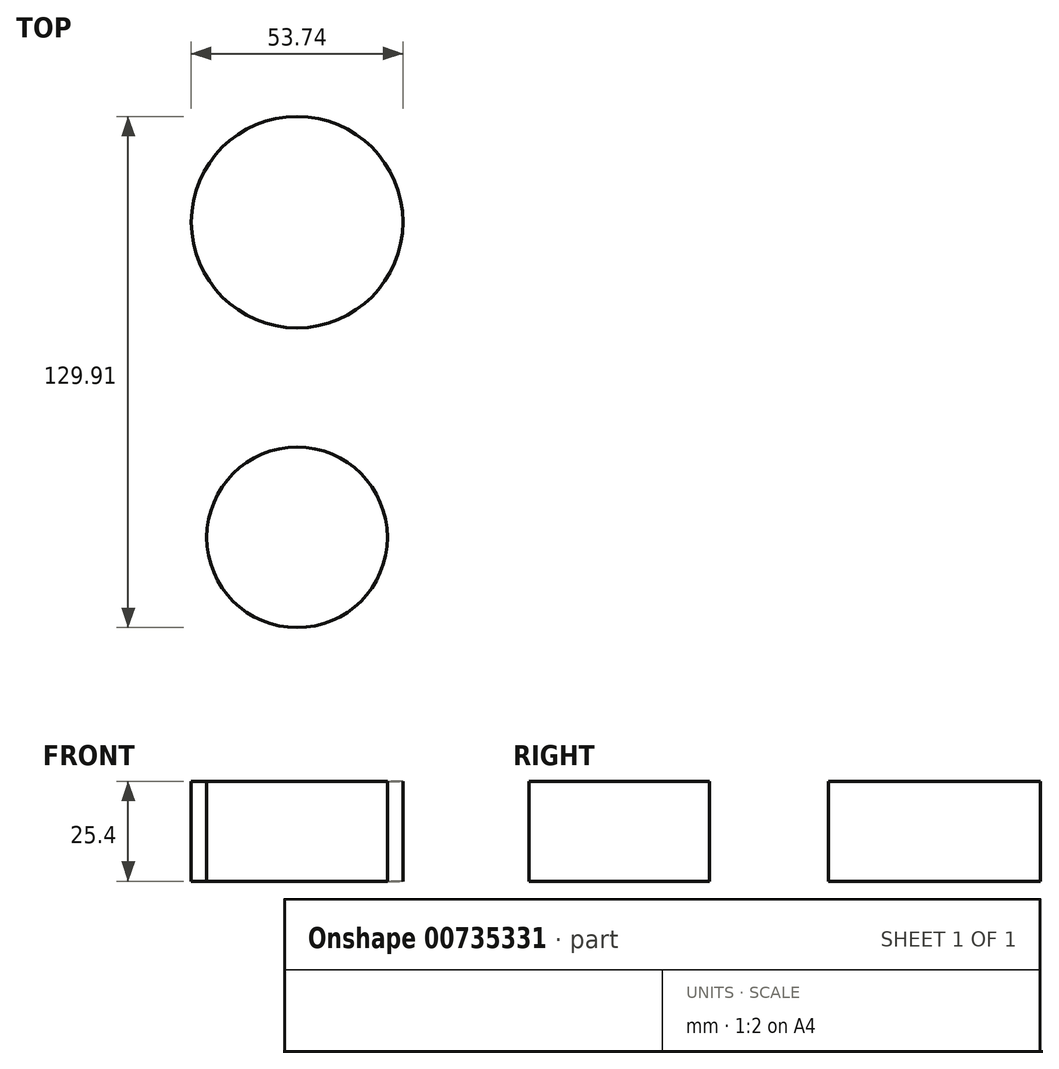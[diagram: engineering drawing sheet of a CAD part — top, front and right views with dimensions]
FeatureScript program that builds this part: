
annotation { "Feature Type Name" : "Feature", "Feature Type Description" : "" }
export const myFeature = defineFeature(function(context is Context, id is Id, definition is map)
    precondition{}
    {
        {
            var Q0;
            Q0=qCreatedBy(makeId("Top.planeOp"),FACE);
            var sketch = newSketch(context, id + "F0", { "sketchPlane" : qUnion([Q0])});
            skCircle(sketch, "E0", {"center": v(0, -43.3) * mm, "radius": 22.93 * mm});
            skCircle(sketch, "E1", {"center": v(0, 30.37) * mm, "radius": 24.48 * mm});
            skSolve(sketch);
        }
        {
            var Q0;
            Q0=makeQuery(id+"F0.imprint","IMPRINT",FACE,{"disambiguationData":[TD([[makeQuery(id+"F0.imprint","IMPRINT",EDGE,{"derivedFrom":sQuery(id+"F0.wireOp",EDGE,"E0")}),1.0]])]});
            extrude(context, id + "F1", {"entities" : qUnion([Q0]), "depth" : 25.4 * mm, "offsetDistance" : 25.4 * mm});
        }
        {
            var Q0;
            Q0=qCreatedBy(makeId("Top.planeOp"),FACE);
            var sketch = newSketch(context, id + "F2", { "sketchPlane" : qUnion([Q0])});
            skCircle(sketch, "E2", {"center": v(0, 36.81) * mm, "radius": 26.87 * mm});
            skSolve(sketch);
        }
        {
            var Q0;
            Q0=makeQuery(id+"F2.imprint","IMPRINT",FACE,{"disambiguationData":[TD([[makeQuery(id+"F2.imprint","IMPRINT",EDGE,{"derivedFrom":sQuery(id+"F2.wireOp",EDGE,"E2")}),1.0]])]});
            var Q1;
            Q1 = qSketchRegion(id + "F2", true);
            extrude(context, id + "F3", {"entities" : qUnion([Q0, Q1]), "depth" : 25.4 * mm, "offsetDistance" : 25.4 * mm});
        }
    });
